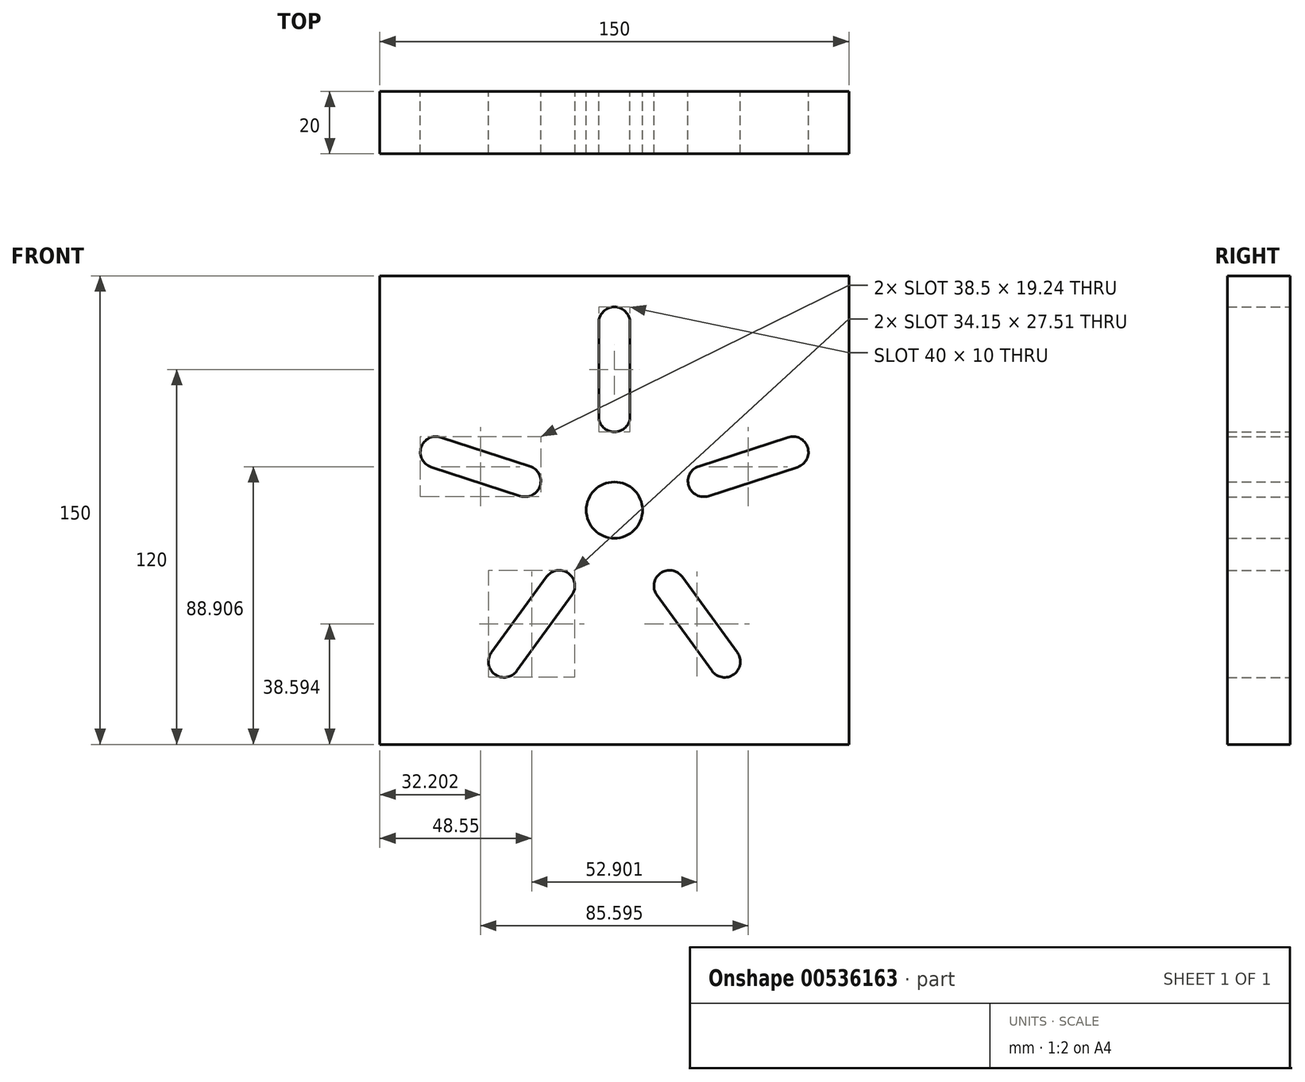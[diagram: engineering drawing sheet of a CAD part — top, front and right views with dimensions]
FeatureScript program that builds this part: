
annotation { "Feature Type Name" : "Feature", "Feature Type Description" : "" }
export const myFeature = defineFeature(function(context is Context, id is Id, definition is map)
    precondition{}
    {
        {
            var Q0;
            Q0=qCreatedBy(makeId("Front.planeOp"),FACE);
            var sketch = newSketch(context, id + "F0", { "sketchPlane" : qUnion([Q0])});
            skLineSegment(sketch, "E0.bottom", {"start": v(75, 75) * mm, "end": v(-75, 75) * mm});
            skLineSegment(sketch, "E0.top", {"start": v(75, -75) * mm, "end": v(-75, -75) * mm});
            skLineSegment(sketch, "E0.left", {"start": v(75, 75) * mm, "end": v(75, -75) * mm});
            skLineSegment(sketch, "E0.right", {"start": v(-75, 75) * mm, "end": v(-75, -75) * mm});
            skPoint(sketch, "E0.middle", {"position": v(0, 0) * mm});
            skCircle(sketch, "E1", {"center": v(0, 0) * mm, "radius": 9 * mm});
            skLineSegment(sketch, "E2", {"start": v(0, 60) * mm, "end": v(0, 30) * mm});
            skArc(sketch, "E3.0.startCap", {"start": v(-5, 60) * mm, "mid": v(0, 65) * mm, "end": v(5, 60) * mm});
            skArc(sketch, "E3.0.endCap", {"start": v(5, 30) * mm, "mid": v(0, 25) * mm, "end": v(-5, 30) * mm});
            skLineSegment(sketch, "E3.0.left", {"start": v(5, 60) * mm, "end": v(5, 30) * mm});
            skLineSegment(sketch, "E3.0.right", {"start": v(-5, 60) * mm, "end": v(-5, 30) * mm});
            skLineSegment(sketch, "E4.1.0", {"start": v(-55.52, 23.3) * mm, "end": v(-26.99, 14.03) * mm});
            skArc(sketch, "E4.1.1", {"start": v(-58.6, 13.79) * mm, "mid": v(-61.82, 20.09) * mm, "end": v(-55.52, 23.3) * mm});
            skLineSegment(sketch, "E4.1.2", {"start": v(-58.6, 13.79) * mm, "end": v(-30.08, 4.52) * mm});
            skArc(sketch, "E4.1.3", {"start": v(-26.99, 14.03) * mm, "mid": v(-23.78, 7.73) * mm, "end": v(-30.08, 4.52) * mm});
            skLineSegment(sketch, "E4.2.0", {"start": v(-39.31, -45.6) * mm, "end": v(-21.68, -21.33) * mm});
            skArc(sketch, "E4.2.1", {"start": v(-31.22, -51.48) * mm, "mid": v(-38.2, -52.59) * mm, "end": v(-39.31, -45.6) * mm});
            skLineSegment(sketch, "E4.2.2", {"start": v(-31.22, -51.48) * mm, "end": v(-13.59, -27.2) * mm});
            skArc(sketch, "E4.2.3", {"start": v(-21.68, -21.33) * mm, "mid": v(-14.7, -20.23) * mm, "end": v(-13.59, -27.2) * mm});
            skLineSegment(sketch, "E4.3.0", {"start": v(31.22, -51.48) * mm, "end": v(13.59, -27.2) * mm});
            skArc(sketch, "E4.3.1", {"start": v(39.31, -45.6) * mm, "mid": v(38.2, -52.59) * mm, "end": v(31.22, -51.48) * mm});
            skLineSegment(sketch, "E4.3.2", {"start": v(39.31, -45.6) * mm, "end": v(21.68, -21.33) * mm});
            skArc(sketch, "E4.3.3", {"start": v(13.59, -27.2) * mm, "mid": v(14.7, -20.23) * mm, "end": v(21.68, -21.33) * mm});
            skLineSegment(sketch, "E4.4.0", {"start": v(58.6, 13.79) * mm, "end": v(30.08, 4.52) * mm});
            skArc(sketch, "E4.4.1", {"start": v(55.52, 23.3) * mm, "mid": v(61.82, 20.09) * mm, "end": v(58.6, 13.79) * mm});
            skLineSegment(sketch, "E4.4.2", {"start": v(55.52, 23.3) * mm, "end": v(26.99, 14.03) * mm});
            skArc(sketch, "E4.4.3", {"start": v(30.08, 4.52) * mm, "mid": v(23.78, 7.73) * mm, "end": v(26.99, 14.03) * mm});
            skSolve(sketch);
        }
        {
            var Q0;
            Q0=makeQuery(id+"F0.imprint","IMPRINT",FACE,{"disambiguationData":[TD([[makeQuery(id+"F0.imprint","IMPRINT",EDGE,{"derivedFrom":sQuery(id+"F0.wireOp",EDGE,"E0.bottom")}),1.0]])]});
            extrude(context, id + "F1", {"entities" : qUnion([Q0]), "depth" : 20 * mm, "offsetDistance" : 25 * mm});
        }
    });
